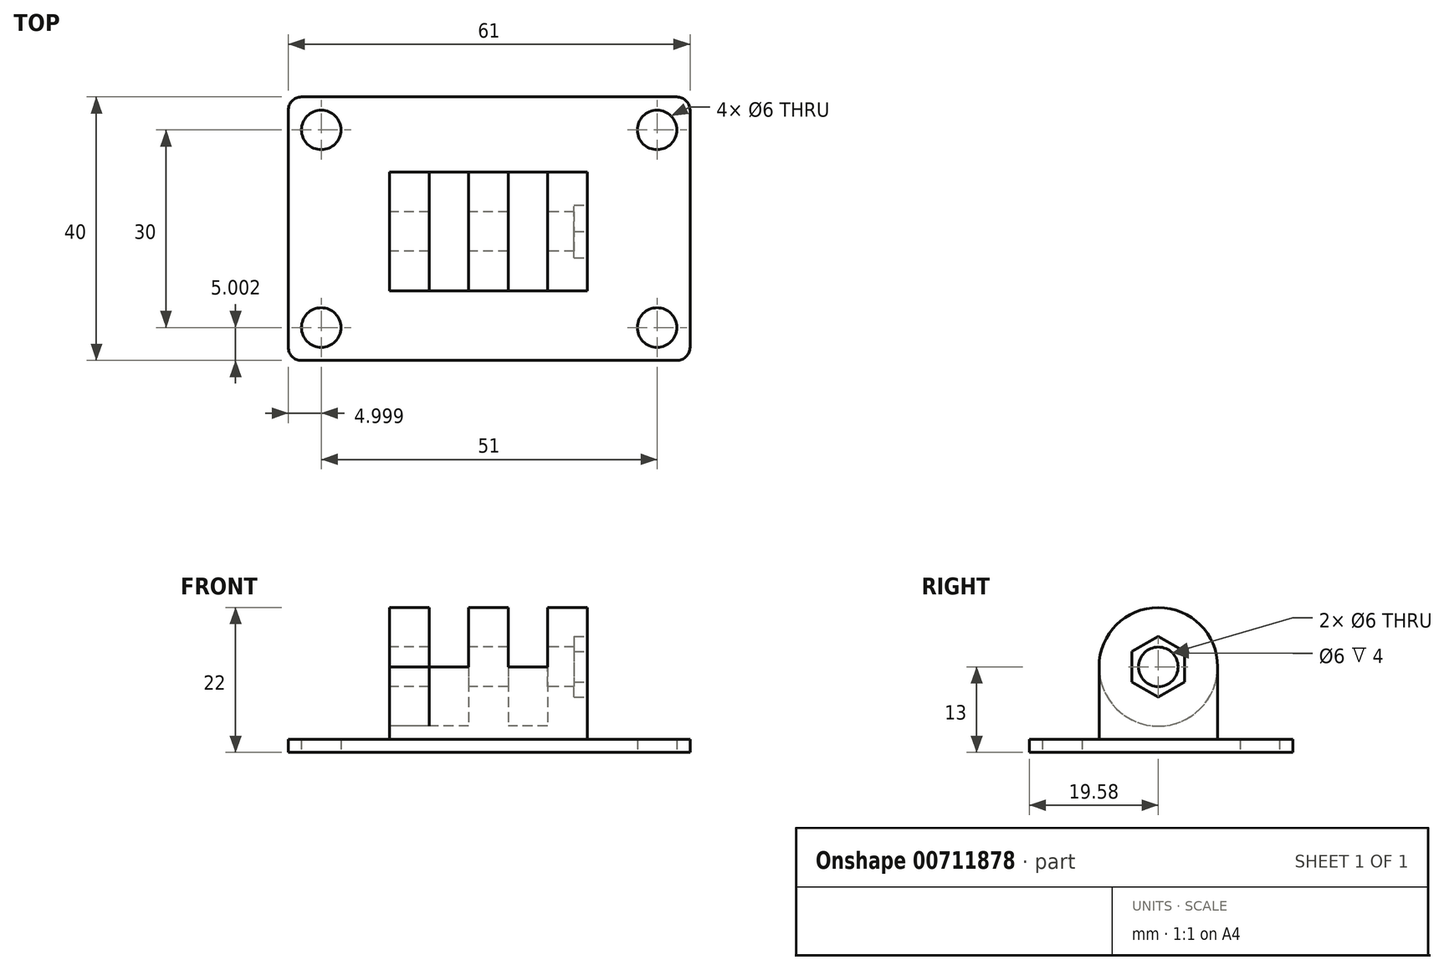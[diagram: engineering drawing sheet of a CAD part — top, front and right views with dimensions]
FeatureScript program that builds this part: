
annotation { "Feature Type Name" : "Feature", "Feature Type Description" : "" }
export const myFeature = defineFeature(function(context is Context, id is Id, definition is map)
    precondition{}
    {
        {
            var Q0;
            Q0=qCreatedBy(makeId("Top.planeOp"),FACE);
            var sketch = newSketch(context, id + "F0", { "sketchPlane" : qUnion([Q0])});
            skLineSegment(sketch, "E0.bottom", {"start": v(-28.38, 20.42) * mm, "end": v(28.62, 20.42) * mm});
            skLineSegment(sketch, "E0.top", {"start": v(-28.38, -19.58) * mm, "end": v(28.62, -19.58) * mm});
            skLineSegment(sketch, "E0.left", {"start": v(-30.38, 18.42) * mm, "end": v(-30.38, -17.58) * mm});
            skLineSegment(sketch, "E0.right", {"start": v(30.62, 18.42) * mm, "end": v(30.62, -17.58) * mm});
            skCircle(sketch, "E1", {"center": v(-25.38, 15.42) * mm, "radius": 3 * mm});
            skCircle(sketch, "E2", {"center": v(-25.38, -14.58) * mm, "radius": 3 * mm});
            skCircle(sketch, "E3", {"center": v(25.62, 15.42) * mm, "radius": 3 * mm});
            skCircle(sketch, "E4", {"center": v(25.62, -14.58) * mm, "radius": 3 * mm});
            skPoint(sketch, "E5.visualSharp", {"position": v(-30.38, 20.42) * mm});
            skArc(sketch, "E5.filletArc", {"start": v(-28.38, 20.42) * mm, "mid": v(-29.8, 19.84) * mm, "end": v(-30.38, 18.42) * mm});
            skPoint(sketch, "E6.visualSharp", {"position": v(30.62, 20.42) * mm});
            skArc(sketch, "E6.filletArc", {"start": v(30.62, 18.42) * mm, "mid": v(30.03, 19.84) * mm, "end": v(28.62, 20.42) * mm});
            skPoint(sketch, "E7.visualSharp", {"position": v(-30.38, -19.58) * mm});
            skArc(sketch, "E7.filletArc", {"start": v(-30.38, -17.58) * mm, "mid": v(-29.8, -19) * mm, "end": v(-28.38, -19.58) * mm});
            skPoint(sketch, "E8.visualSharp", {"position": v(30.62, -19.58) * mm});
            skArc(sketch, "E8.filletArc", {"start": v(28.62, -19.58) * mm, "mid": v(30.03, -19) * mm, "end": v(30.62, -17.58) * mm});
            skSolve(sketch);
        }
        {
            var Q0;
            Q0 = qSketchRegion(id + "FlYgRnEniIu7ZzQ_0", true);
            var Q1;
            Q1=makeQuery(id+"F0.imprint","IMPRINT",FACE,{"disambiguationData":[TD([[makeQuery(id+"F0.imprint","IMPRINT",EDGE,{"derivedFrom":sQuery(id+"F0.wireOp",EDGE,"E0.bottom")}),-1.0]])]});
            extrude(context, id + "F1", {"entities" : qUnion([Q0, Q1]), "depth" : 2 * mm, "offsetDistance" : 25.4 * mm});
        }
        {
            var Q0;
            Q0=makeQuery(id+"F1.opExtrude","CAP_FACE",FACE,{"disambiguationData":[OSD([sQuery(id+"F0.wireOp",EDGE,"E0.bottom"),sQuery(id+"F0.wireOp",EDGE,"E0.top"),sQuery(id+"F0.wireOp",EDGE,"E0.left"),sQuery(id+"F0.wireOp",EDGE,"E0.right"),sQuery(id+"F0.wireOp",EDGE,"E1"),sQuery(id+"F0.wireOp",EDGE,"E2"),sQuery(id+"F0.wireOp",EDGE,"E3"),sQuery(id+"F0.wireOp",EDGE,"E4"),sQuery(id+"F0.wireOp",EDGE,"E5.filletArc"),sQuery(id+"F0.wireOp",EDGE,"E6.filletArc"),sQuery(id+"F0.wireOp",EDGE,"E7.filletArc"),sQuery(id+"F0.wireOp",EDGE,"E8.filletArc")])],"isStart":false});
            var sketch = newSketch(context, id + "F2", { "sketchPlane" : qUnion([Q0])});
            skLineSegment(sketch, "E9.bottom", {"start": v(-15, 9) * mm, "end": v(15, 9) * mm});
            skLineSegment(sketch, "E9.top", {"start": v(-15, -9) * mm, "end": v(15, -9) * mm});
            skLineSegment(sketch, "E9.left", {"start": v(-15, 9) * mm, "end": v(-15, -9) * mm});
            skLineSegment(sketch, "E9.right", {"start": v(15, 9) * mm, "end": v(15, -9) * mm});
            skPoint(sketch, "E9.middle", {"position": v(0, 0) * mm});
            skSolve(sketch);
        }
        {
            var Q0;
            Q0 = qSketchRegion(id + "F2", true);
            extrude(context, id + "F3", {"entities" : qUnion([Q0]), "operationType" : NewBodyOperationType.ADD, "depth" : 20 * mm, "offsetDistance" : 25.4 * mm});
        }
        {
            var Q0;
            Q0=makeQuery(id+"F3.opExtrude","SWEPT_FACE",FACE,{"disambiguationData":[OSD([sQuery(id+"F2.wireOp",EDGE,"E9.left")])]});
            var sketch = newSketch(context, id + "F4", { "sketchPlane" : qUnion([Q0])});
            skCircle(sketch, "E10", {"center": v(0, 13) * mm, "radius": 9 * mm});
            skLineSegment(sketch, "E11", {"start": v(9, 22) * mm, "end": v(9, 2) * mm});
            skLineSegment(sketch, "E12", {"start": v(-9, 22) * mm, "end": v(9, 22) * mm});
            skLineSegment(sketch, "E13", {"start": v(-9, 22) * mm, "end": v(-9, 2) * mm});
            skLineSegment(sketch, "E14", {"start": v(-9, 2) * mm, "end": v(9, 2) * mm});
            skLineSegment(sketch, "E15.0.1", {"start": v(9, 2) * mm, "end": v(9, 22) * mm});
            skLineSegment(sketch, "E15.0.2", {"start": v(9, 22) * mm, "end": v(-9, 22) * mm});
            skPoint(sketch, "E16.startSnap0", {"position": v(-9, 12) * mm});
            skSolve(sketch);
        }
        {
            var Q0;
            Q0=makeQuery(id+"F3.opExtrude","SWEPT_FACE",FACE,{"disambiguationData":[OSD([sQuery(id+"F2.wireOp",EDGE,"E9.left")])]});
            var sketch = newSketch(context, id + "F5", { "sketchPlane" : qUnion([Q0])});
            skLineSegment(sketch, "E17", {"start": v(-9, 22) * mm, "end": v(-9, 2) * mm});
            skLineSegment(sketch, "E18", {"start": v(9, 22) * mm, "end": v(9, 2) * mm});
            skLineSegment(sketch, "E19", {"start": v(-9, 22) * mm, "end": v(9, 22) * mm});
            skLineSegment(sketch, "E20", {"start": v(-9, 2) * mm, "end": v(9, 2) * mm});
            skArc(sketch, "E21", {"start": v(0, 22) * mm, "mid": v(-6.36, 19.36) * mm, "end": v(-9, 13) * mm});
            skLineSegment(sketch, "E22", {"start": v(-9, 22) * mm, "end": v(0, 22) * mm});
            skLineSegment(sketch, "E23", {"start": v(-9, 22) * mm, "end": v(-9, 13) * mm});
            skArc(sketch, "E24", {"start": v(9, 13) * mm, "mid": v(6.36, 19.36) * mm, "end": v(0, 22) * mm});
            skLineSegment(sketch, "E25", {"start": v(9, 22) * mm, "end": v(9, 13) * mm});
            skLineSegment(sketch, "E26", {"start": v(0, 22) * mm, "end": v(9, 22) * mm});
            skSolve(sketch);
        }
        {
            var Q0;
            Q0=makeQuery(id+"F5.imprint","IMPRINT",FACE,{"disambiguationData":[TD([[makeQuery(id+"F5.imprint","IMPRINT",EDGE,{"derivedFrom":sQuery(id+"F5.wireOp",EDGE,"E24")}),-1.0]])]});
            var Q1;
            {var subQ0=sQuery(id+"F4.wireOp",EDGE,"E15.0.2");var subQ1=sQuery(id+"F4.wireOp",EDGE,"E10");var subQ2=makeQuery(id+"F4.imprint","INTERSECT",VERTEX,{"derivedFrom":[subQ1,subQ0]});Q1=makeQuery(id+"F4.imprint","IMPRINT",FACE,{"disambiguationData":[TD([[makeQuery(id+"F4.imprint","IMPRINT",EDGE,{"disambiguationData":[TD([[subQ2,-1.0]])],"derivedFrom":subQ1}),-1.0]])]});}
            extrude(context, id + "F6", {"entities" : qUnion([Q0, Q1]), "operationType" : NewBodyOperationType.REMOVE, "oppositeDirection" : true, "depth" : 30 * mm, "offsetDistance" : 25.4 * mm});
        }
        {
            var Q0;
            Q0=makeQuery(id+"F3.opExtrude","SWEPT_FACE",FACE,{"disambiguationData":[OSD([sQuery(id+"F2.wireOp",EDGE,"E9.left")])]});
            var sketch = newSketch(context, id + "F7", { "sketchPlane" : qUnion([Q0])});
            skCircle(sketch, "E27", {"center": v(0, 13) * mm, "radius": 9 * mm});
            skSolve(sketch);
        }
        {
            var Q0;
            Q0 = qSketchRegion(id + "F7", true);
            extrude(context, id + "F8", {"entities" : qUnion([Q0]), "operationType" : NewBodyOperationType.REMOVE, "oppositeDirection" : true, "depth" : 30 * mm, "offsetDistance" : 25.4 * mm});
        }
        {
            var Q0;
            Q0=makeQuery(id+"F3.opExtrude","SWEPT_FACE",FACE,{"disambiguationData":[OSD([sQuery(id+"F2.wireOp",EDGE,"E9.left")])]});
            var sketch = newSketch(context, id + "F9", { "sketchPlane" : qUnion([Q0])});
            skCircle(sketch, "E28", {"center": v(0, 13) * mm, "radius": 9 * mm});
            skSolve(sketch);
        }
        {
            var Q0;
            Q0=makeQuery(id+"F3.opExtrude","SWEPT_FACE",FACE,{"disambiguationData":[OSD([sQuery(id+"F2.wireOp",EDGE,"E9.right")])]});
            var sketch = newSketch(context, id + "F10", { "sketchPlane" : qUnion([Q0])});
            skCircle(sketch, "E29", {"center": v(0, 13) * mm, "radius": 9 * mm});
            skSolve(sketch);
        }
        {
            var Q0;
            Q0 = qSketchRegion(id + "F10", true);
            extrude(context, id + "F11", {"entities" : qUnion([Q0]), "operationType" : NewBodyOperationType.ADD, "oppositeDirection" : true, "depth" : 6 * mm, "offsetDistance" : 25.4 * mm});
        }
        {
            var Q0;
            Q0=makeQuery(id+"F11.opExtrude","CAP_FACE",FACE,{"disambiguationData":[OSD([sQuery(id+"F10.wireOp",EDGE,"E29")])],"isStart":false});
            var sketch = newSketch(context, id + "F12", { "sketchPlane" : qUnion([Q0])});
            skCircle(sketch, "E30", {"center": v(0, 13) * mm, "radius": 9 * mm});
            skSolve(sketch);
        }
        {
            var Q0;
            Q0 = qSketchRegion(id + "F12", true);
            extrude(context, id + "F13", {"entities" : qUnion([Q0]), "operationType" : NewBodyOperationType.ADD, "depth" : 18 * mm, "offsetDistance" : 25.4 * mm, "hasSecondDirection" : true, "secondDirectionOppositeDirection" : false, "secondDirectionDepth" : 6 * mm});
        }
        {
            var Q0;
            Q0=makeQuery(id+"F13.opExtrude","CAP_FACE",FACE,{"disambiguationData":[OSD([sQuery(id+"F12.wireOp",EDGE,"E30")])],"isStart":false});
            extrude(context, id + "F14", {"entities" : qUnion([Q0]), "operationType" : NewBodyOperationType.REMOVE, "oppositeDirection" : true, "depth" : 6 * mm, "offsetDistance" : 25.4 * mm});
        }
        {
            var Q0;
            {var subQ0=sQuery(id+"F9.wireOp",EDGE,"E28");var subQ1=sQuery(id+"F2.wireOp",EDGE,"E9.left");var subQ2=makeQuery(id+"F9.imprint","INTERSECT",VERTEX,{"derivedFrom":[makeQuery(id+"F3.opExtrude","SWEPT_EDGE",EDGE,{"disambiguationData":[OSD([sQuery(id+"F2.wireOp",EDGE,"E9.bottom"),subQ1])]}),subQ0]});Q0=makeQuery(id+"F9.imprint","IMPRINT",FACE,{"disambiguationData":[TD([[makeQuery(id+"F9.imprint","IMPRINT",EDGE,{"disambiguationData":[TD([[subQ2,1.0]])],"derivedFrom":subQ0}),1.0]])]});}
            extrude(context, id + "F15", {"entities" : qUnion([Q0]), "oppositeDirection" : true, "depth" : 6 * mm, "offsetDistance" : 25.4 * mm});
        }
        {
            var Q0;
            Q0=makeQuery(id+"F15.opExtrude","CAP_FACE",FACE,{"disambiguationData":[OSD([sQuery(id+"F9.wireOp",EDGE,"E28")])],"isStart":true});
            var sketch = newSketch(context, id + "F16", { "sketchPlane" : qUnion([Q0])});
            skCircle(sketch, "E31", {"center": v(0, 13) * mm, "radius": 3 * mm});
            skSolve(sketch);
        }
        {
            var Q0;
            Q0 = qSketchRegion(id + "F16", true);
            extrude(context, id + "F17", {"entities" : qUnion([Q0]), "operationType" : NewBodyOperationType.REMOVE, "oppositeDirection" : true, "depth" : 30 * mm, "offsetDistance" : 25.4 * mm});
        }
        {
            var Q0;
            Q0=makeQuery(id+"F11.boolean.opBoolean","MERGE",FACE,{"derivedFrom":[makeQuery(id+"F3.opExtrude","SWEPT_FACE",FACE,{"disambiguationData":[OSD([sQuery(id+"F2.wireOp",EDGE,"E9.right")])]}),makeQuery(id+"F11.opExtrude","CAP_FACE",FACE,{"disambiguationData":[OSD([sQuery(id+"F10.wireOp",EDGE,"E29")])],"isStart":true})]});
            var sketch = newSketch(context, id + "F18", { "sketchPlane" : qUnion([Q0])});
            skCircle(sketch, "E32.cCircle", {"center": v(0, 13) * mm, "radius": 4 * mm, "construction": true});
            skLineSegment(sketch, "E32.0", {"start": v(4, 15.3) * mm, "end": v(4, 10.7) * mm});
            skLineSegment(sketch, "E32.1", {"start": v(4, 10.7) * mm, "end": v(0, 8.38) * mm});
            skLineSegment(sketch, "E32.2", {"start": v(0, 8.38) * mm, "end": v(-4, 10.7) * mm});
            skLineSegment(sketch, "E32.3", {"start": v(-4, 10.7) * mm, "end": v(-4, 15.3) * mm});
            skLineSegment(sketch, "E32.4", {"start": v(-4, 15.3) * mm, "end": v(0, 17.62) * mm});
            skLineSegment(sketch, "E32.5", {"start": v(0, 17.62) * mm, "end": v(4, 15.3) * mm});
            skPoint(sketch, "E32.0.midPoint", {"position": v(4, 13) * mm});
            skSolve(sketch);
        }
        {
            var Q0;
            Q0=makeQuery(id+"F18.imprint","IMPRINT",FACE,{"disambiguationData":[TD([[makeQuery(id+"F18.imprint","IMPRINT",EDGE,{"derivedFrom":sQuery(id+"F18.wireOp",EDGE,"E32.0")}),-1.0]])]});
            extrude(context, id + "F19", {"entities" : qUnion([Q0]), "operationType" : NewBodyOperationType.REMOVE, "oppositeDirection" : true, "depth" : 2 * mm, "offsetDistance" : 25.4 * mm});
        }
    });
